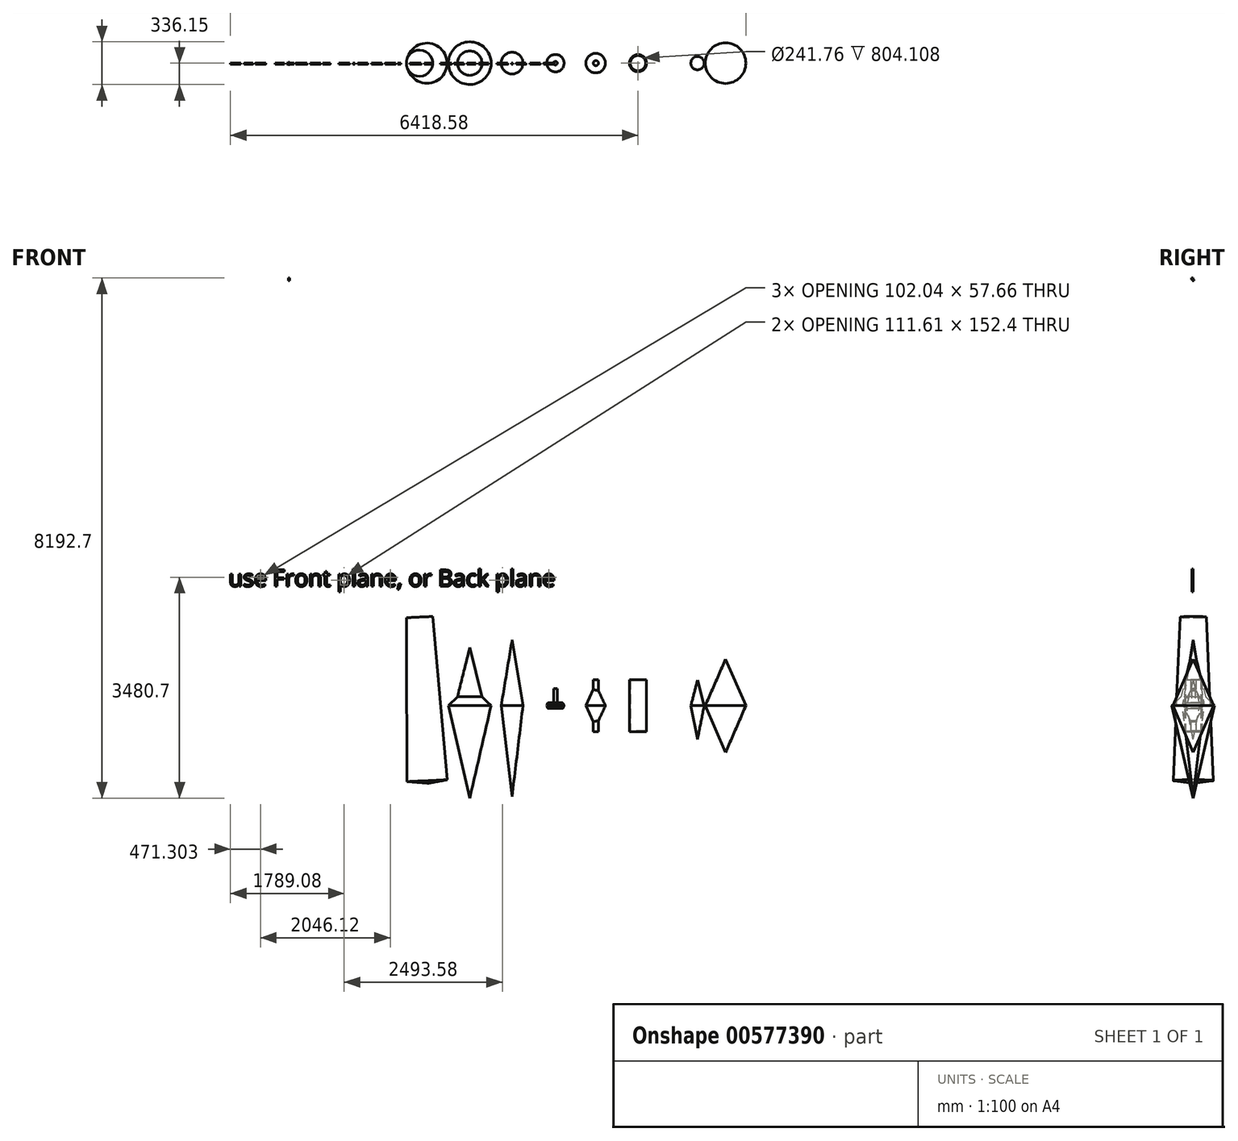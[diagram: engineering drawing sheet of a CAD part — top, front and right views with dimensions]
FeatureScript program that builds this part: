
annotation { "Feature Type Name" : "Feature", "Feature Type Description" : "" }
export const myFeature = defineFeature(function(context is Context, id is Id, definition is map)
    precondition{}
    {
        {
            var Q0;
            Q0=qCreatedBy(makeId("Top.planeOp"),FACE);
            var sketch = newSketch(context, id + "F0", { "sketchPlane" : qUnion([Q0])});
            skCircle(sketch, "E0", {"center": v(0, 0) * mm, "radius": 137.28 * mm});
            skSolve(sketch);
        }
        {
            var Q0;
            Q0=makeQuery(id+"F0.imprint","IMPRINT",FACE,{"disambiguationData":[TD([[makeQuery(id+"F0.imprint","IMPRINT",EDGE,{"derivedFrom":sQuery(id+"F0.wireOp",EDGE,"E0")}),1.0]])]});
            extrude(context, id + "F1", {"entities" : qUnion([Q0]), "endBound" : BoundingType.SYMMETRIC, "depth" : 88.63 * mm, "offsetDistance" : 25.4 * mm, "hasDraft" : true, "draftAngle" : 24 * degree, "draftPullDirection" : true});
        }
        {
            var Q0;
            Q0=qCreatedBy(makeId("Top.planeOp"),FACE);
            var sketch = newSketch(context, id + "F2", { "sketchPlane" : qUnion([Q0])});
            skCircle(sketch, "E1", {"center": v(0, 0) * mm, "radius": 29.68 * mm});
            skSolve(sketch);
        }
        {
            var Q0;
            Q0 = qSketchRegion(id + "F2", true);
            extrude(context, id + "F3", {"entities" : qUnion([Q0]), "operationType" : NewBodyOperationType.ADD, "depth" : 266.7 * mm, "offsetDistance" : 25.4 * mm});
        }
        {
            var Q0;
            Q0=makeQuery(id+"F1.opExtrude","CAP_EDGE",EDGE,{"disambiguationData":[OSD([sQuery(id+"F0.wireOp",EDGE,"E0")])],"isStart":false});
            var Q1;
            Q1=makeQuery(id+"F1.opExtrude","CAP_EDGE",EDGE,{"disambiguationData":[OSD([sQuery(id+"F0.wireOp",EDGE,"E0")])],"isStart":true});
            fillet(context, id + "F4", {"entities" : qUnion([Q0, Q1]), "radius" : 9.52 * mm, "tangentPropagation" : true, "allowEdgeOverflow" : false});
        }
        {
            var Q0;
            Q0=qCreatedBy(makeId("Top.planeOp"),FACE);
            var sketch = newSketch(context, id + "F5", { "sketchPlane" : qUnion([Q0])});
            skCircle(sketch, "E2", {"center": v(634.2, 0) * mm, "radius": 153.83 * mm});
            skSolve(sketch);
        }
        {
            var Q0;
            Q0 = qSketchRegion(id + "F5", true);
            extrude(context, id + "F6", {"entities" : qUnion([Q0]), "endBound" : BoundingType.SYMMETRIC, "depth" : 651.78 * mm, "offsetDistance" : 25.4 * mm, "hasDraft" : true, "draftAngle" : 24.9 * degree, "draftPullDirection" : true});
        }
        {
            var Q0;
            Q0=qCreatedBy(makeId("Top.planeOp"),FACE);
            var sketch = newSketch(context, id + "F7", { "sketchPlane" : qUnion([Q0])});
            skCircle(sketch, "E3", {"center": v(1301.28, 0) * mm, "radius": 135.17 * mm});
            skCircle(sketch, "E4", {"center": v(638.1, 0) * mm, "radius": 40.19 * mm});
            skSolve(sketch);
        }
        {
            var Q0;
            Q0 = qSketchRegion(id + "F7", true);
            extrude(context, id + "F8", {"entities" : qUnion([Q0]), "operationType" : NewBodyOperationType.ADD, "endBound" : BoundingType.SYMMETRIC, "depth" : 818.4 * mm, "offsetDistance" : 25.4 * mm});
        }
        {
            var Q0;
            Q0=makeQuery(id+"F8.opExtrude","CAP_FACE",FACE,{"disambiguationData":[OSD([sQuery(id+"F7.wireOp",EDGE,"E3")])],"isStart":false});
            shell(context, id + "F9", {"entities" : qUnion([Q0]), "thickness" : 14.29 * mm});
        }
        {
            var Q0;
            Q0=qCreatedBy(makeId("Front.planeOp"),FACE);
            var sketch = newSketch(context, id + "F10", { "sketchPlane" : qUnion([Q0])});
            skLineSegment(sketch, "E5", {"start": v(2238.3, 401.47) * mm, "end": v(2238.3, -530.18) * mm});
            skLineSegment(sketch, "E6", {"start": v(2238.3, -530.18) * mm, "end": v(2343.43, 0) * mm});
            skLineSegment(sketch, "E7", {"start": v(2343.43, 0) * mm, "end": v(2238.3, 401.47) * mm});
            skSolve(sketch);
        }
        {
            var Q0;
            Q0 = qSketchRegion(id + "F10", true);
            var Q1;
            Q1=sQuery(id+"F10.wireOp",EDGE,"E5");
            revolve(context, id + "F11", {"entities" : qUnion([Q0]), "axis" : qUnion([Q1]), "revolveType" : RevolveType.FULL});
        }
        {
            var Q0;
            Q0=qCreatedBy(makeId("Front.planeOp"),FACE);
            var sketch = newSketch(context, id + "F12", { "sketchPlane" : qUnion([Q0])});
            skLineSegment(sketch, "E8", {"start": v(-682.49, 1034.5) * mm, "end": v(-682.49, -1432.46) * mm});
            skLineSegment(sketch, "E9", {"start": v(-682.49, -1432.46) * mm, "end": v(-853.47, 0) * mm});
            skLineSegment(sketch, "E10", {"start": v(-853.47, 0) * mm, "end": v(-682.49, 1034.5) * mm});
            skSolve(sketch);
        }
        {
            var Q0;
            Q0 = qSketchRegion(id + "F12", true);
            var Q1;
            Q1=sQuery(id+"F12.wireOp",EDGE,"E8");
            revolve(context, id + "F13", {"entities" : qUnion([Q0]), "axis" : qUnion([Q1]), "revolveType" : RevolveType.FULL});
        }
        {
            var Q0;
            Q0=qCreatedBy(makeId("Front.planeOp"),FACE);
            var sketch = newSketch(context, id + "F14", { "sketchPlane" : qUnion([Q0])});
            skLineSegment(sketch, "E11", {"start": v(-1348.94, 916.13) * mm, "end": v(-1348.94, -1456.32) * mm});
            skLineSegment(sketch, "E12", {"start": v(-1348.94, -1456.32) * mm, "end": v(-1685.09, 0) * mm});
            skLineSegment(sketch, "E13", {"start": v(-1685.09, 0) * mm, "end": v(-1541.42, 140.64) * mm});
            skLineSegment(sketch, "E14", {"start": v(-1541.42, 140.64) * mm, "end": v(-1348.94, 916.13) * mm});
            skSolve(sketch);
        }
        {
            var Q0;
            Q0 = qSketchRegion(id + "F14", true);
            var Q1;
            Q1=sQuery(id+"F14.wireOp",EDGE,"E11");
            revolve(context, id + "F15", {"entities" : qUnion([Q0]), "axis" : qUnion([Q1]), "revolveType" : RevolveType.FULL});
        }
        {
            var Q0;
            Q0=qCreatedBy(makeId("Front.planeOp"),FACE);
            var sketch = newSketch(context, id + "F16", { "sketchPlane" : qUnion([Q0])});
            skLineSegment(sketch, "E15", {"start": v(-2020.1, -1226.53) * mm, "end": v(-2140.73, 1395.42) * mm});
            skLineSegment(sketch, "E16", {"start": v(-2140.73, 1395.42) * mm, "end": v(-2347.64, 1385.9) * mm});
            skLineSegment(sketch, "E17", {"start": v(-2347.64, 1385.9) * mm, "end": v(-2337.9, -1196.08) * mm});
            skLineSegment(sketch, "E18", {"start": v(-2337.9, -1196.08) * mm, "end": v(-2020.1, -1226.53) * mm});
            skSolve(sketch);
        }
        {
            var Q0;
            Q0 = qSketchRegion(id + "F16", true);
            var Q1;
            Q1=sQuery(id+"F16.wireOp",EDGE,"E15");
            revolve(context, id + "F17", {"entities" : qUnion([Q0]), "axis" : qUnion([Q1]), "revolveType" : RevolveType.FULL});
        }
        {
            var Q0;
            Q0=qCreatedBy(makeId("Front.planeOp"),FACE);
            var sketch = newSketch(context, id + "F18", { "sketchPlane" : qUnion([Q0])});
            skFitSpline(sketch, "E19", {"points": [v(-3218, 1332.68) * mm, v(-3279, -205.96) * mm, v(-3162.56, -1198.8) * mm, v(-3534.05, -1217.87) * mm, v(-3578.41, -204.58) * mm, v(-3814.06, 1576.12) * mm, v(-3218, 1332.68) * mm]});
            skLineSegment(sketch, "E20", {"start": v(-3162.56, 2287.13) * mm, "end": v(-2771.85, -1484.98) * mm, "construction": true});
            skSolve(sketch);
        }
        {
            var Q0;
            Q0=sQuery(id+"F18.wireOp",EDGE,"E19");
            var Q1;
            Q1=sQuery(id+"F18.wireOp",EDGE,"E20");
            revolve(context, id + "F19", {"bodyType" : ToolBodyType.SURFACE, "surfaceEntities" : qUnion([Q0]), "axis" : qUnion([Q1]), "revolveType" : RevolveType.FULL});
        }
        {
            var Q0;
            Q0=qCreatedBy(makeId("Front.planeOp"),FACE);
            var sketch = newSketch(context, id + "F20", { "sketchPlane" : qUnion([Q0])});
            skLineSegment(sketch, "E21", {"start": v(2680.65, 0) * mm, "end": v(2680.65, 734.65) * mm});
            skLineSegment(sketch, "E22", {"start": v(2680.65, 734.65) * mm, "end": v(3000.12, 0) * mm});
            skLineSegment(sketch, "E23", {"start": v(3000.12, 0) * mm, "end": v(2680.65, 0) * mm});
            skLineSegment(sketch, "E24.MirrorCS", {"start": v(2680.65, -734.65) * mm, "end": v(3000.12, 0) * mm});
            skLineSegment(sketch, "E25.MirrorCS", {"start": v(2680.65, 0) * mm, "end": v(2680.65, -734.65) * mm});
            skSolve(sketch);
        }
        {
            var Q0;
            Q0 = qSketchRegion(id + "F20", true);
            var Q1;
            Q1=sQuery(id+"F20.wireOp",EDGE,"E21");
            revolve(context, id + "F21", {"entities" : qUnion([Q0]), "axis" : qUnion([Q1]), "revolveType" : RevolveType.FULL});
        }
        {
            var Q0;
            Q0=qCreatedBy(makeId("Front.planeOp"),FACE);
            var sketch = newSketch(context, id + "F22", { "sketchPlane" : qUnion([Q0])});
            skText(sketch, "E26", { "text": "use Front plane, or Back plane", "fontName": "OpenSans-Regular.ttf"});
            const initialGuessF22  = {"E26": [-5.14653, 1.87927, 1, 0, 0.26253]};
            skSetInitialGuess(sketch, initialGuessF22);
            skSolve(sketch);
        }
        {
            var Q0;
            Q0 = qSketchRegion(id + "F22", true);
            extrude(context, id + "F23", {"entities" : qUnion([Q0]), "depth" : 20.64 * mm, "offsetDistance" : 25.4 * mm});
        }
        {
            var Q0;
            Q0=qCreatedBy(makeId("Front.planeOp"),FACE);
            var sketch = newSketch(context, id + "F24", { "sketchPlane" : qUnion([Q0])});
            skLineSegment(sketch, "E27.bottom", {"start": v(-4203.85, 6695.1) * mm, "end": v(-4183.21, 6695.1) * mm});
            skLineSegment(sketch, "E27.top", {"start": v(-4203.85, 6736.38) * mm, "end": v(-4183.21, 6736.38) * mm});
            skLineSegment(sketch, "E27.left", {"start": v(-4203.85, 6695.1) * mm, "end": v(-4203.85, 6736.38) * mm});
            skLineSegment(sketch, "E27.right", {"start": v(-4183.21, 6695.1) * mm, "end": v(-4183.21, 6736.38) * mm});
            skLineSegment(sketch, "E28", {"start": v(-4183.21, 6715.75) * mm, "end": v(-4203.85, 6715.75) * mm});
            skSolve(sketch);
        }
        {
            var Q0;
            {var subQ0=sQuery(id+"F24.wireOp",EDGE,"E27.top");Q0=makeQuery(id+"F24.imprint","IMPRINT",FACE,{"disambiguationData":[TD([[makeQuery(id+"F24.imprint","IMPRINT",EDGE,{"derivedFrom":subQ0}),-1.0]])]});}
            extrude(context, id + "F25", {"entities" : qUnion([Q0]), "depth" : 25.4 * mm, "offsetDistance" : 25.4 * mm});
        }
        {
            var Q0;
            {var subQ0=sQuery(id+"F24.wireOp",EDGE,"E27.bottom");Q0=makeQuery(id+"F24.imprint","IMPRINT",FACE,{"disambiguationData":[TD([[makeQuery(id+"F24.imprint","IMPRINT",EDGE,{"derivedFrom":subQ0}),1.0]])]});}
            extrude(context, id + "F26", {"entities" : qUnion([Q0]), "endBound" : BoundingType.SYMMETRIC, "depth" : 25.4 * mm, "offsetDistance" : 25.4 * mm});
        }
    });
